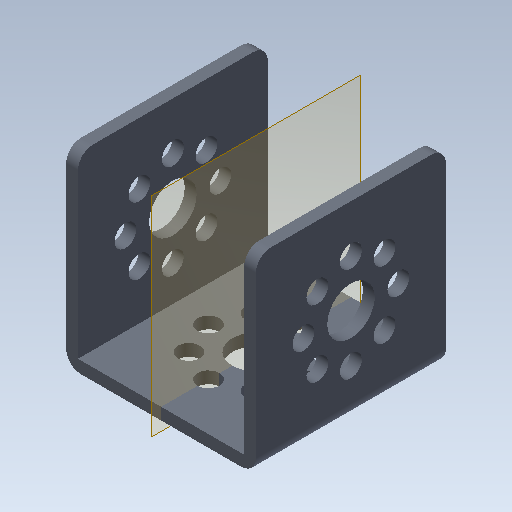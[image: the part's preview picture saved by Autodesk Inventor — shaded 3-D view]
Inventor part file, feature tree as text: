
AUTODESK INVENTOR PART (.ipt)
format: ipt  version: 2020 (Build 240168000, 168)  size: 219,136 bytes
history: native  units: in
note: dims shown in document units (in); Inventor stores cm internally (conversion verified against a paired STEP export)
features: other x23, plane x1, imported_body x1
ambient origin geometry x8: Origin, YZ Plane, XZ Plane, XY Plane, X Axis, Y Axis, Z Axis, Center Point
bodies: Body1 (feature_tree)
feature tree (25):
  other  "tetrix_739065_2012"
  other  "tetrix_739065_20121"
  other  "A_1"
  other  "A_18"
  other  "A_10"
  other  "A_11"
  other  "A_12"
  other  "A_13"
  other  "A_14"
  other  "A_15"
  other  "A_16"
  other  "A_17"
  other  "A_19"
  other  "A_20"
  other  "A_21"
  other  "A_22"
  other  "A_23"
  other  "A_24"
  other  "A_25"
  other  "A_26"
  other  "FRONT"
  other  "TOP"
  other  "RIGHT"
  plane  "Work Plane4"
  imported_body  "Base1"
